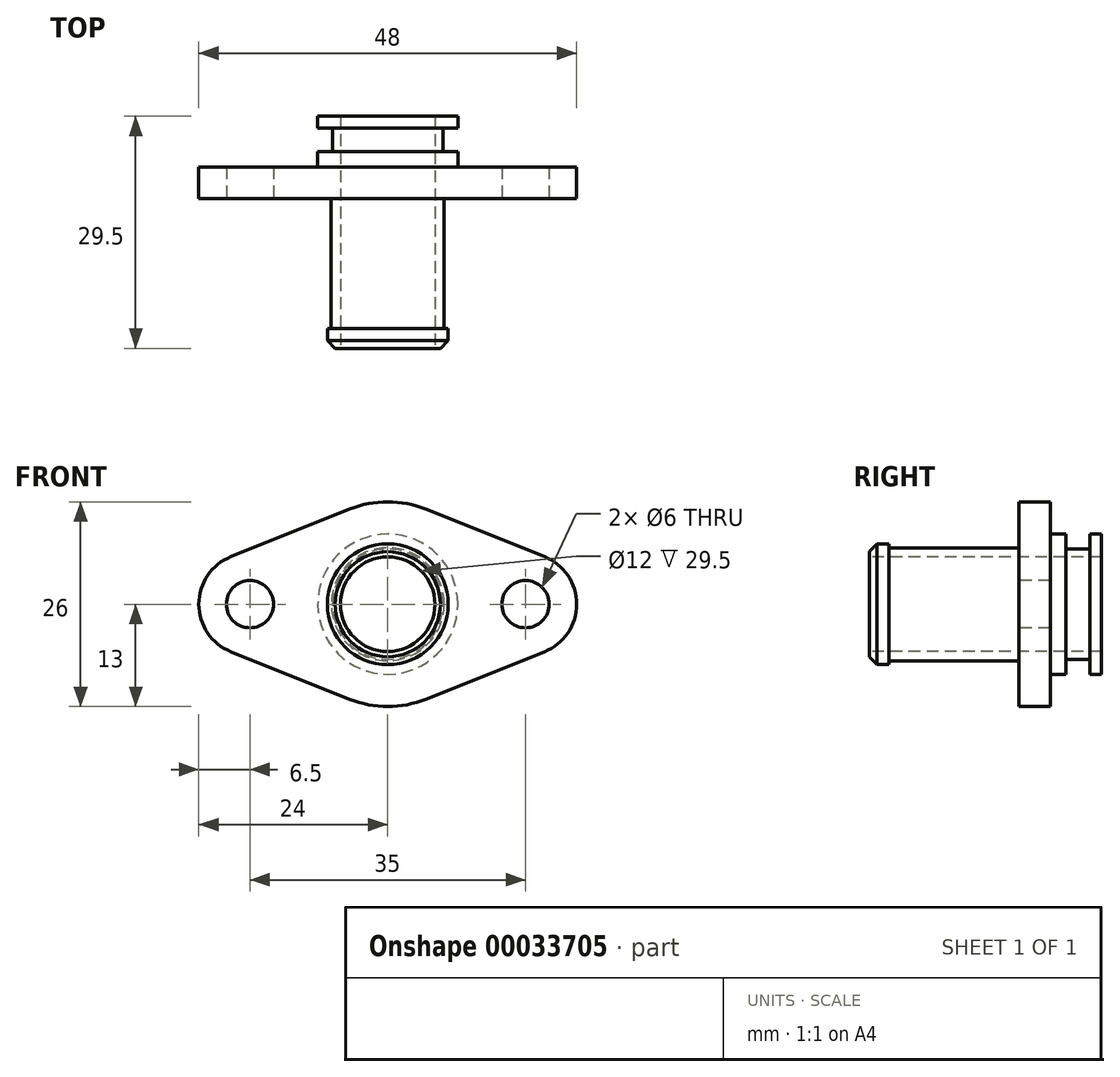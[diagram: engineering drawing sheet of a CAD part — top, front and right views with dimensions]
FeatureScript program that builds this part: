
annotation { "Feature Type Name" : "Feature", "Feature Type Description" : "" }
export const myFeature = defineFeature(function(context is Context, id is Id, definition is map)
    precondition{}
    {
        {
            var Q0;
            Q0=qCreatedBy(makeId("Right.planeOp"),FACE);
            var sketch = newSketch(context, id + "F0", { "sketchPlane" : qUnion([Q0])});
            skLineSegment(sketch, "E0", {"start": v(-19, 0) * mm, "end": v(11.7, 0) * mm, "construction": true});
            skLineSegment(sketch, "E1", {"start": v(-19, 6) * mm, "end": v(10.5, 6) * mm});
            skLineSegment(sketch, "E2", {"start": v(10.5, 6) * mm, "end": v(10.5, 8.9) * mm});
            skLineSegment(sketch, "E3", {"start": v(10.5, 8.9) * mm, "end": v(9, 8.9) * mm});
            skLineSegment(sketch, "E4", {"start": v(9, 8.9) * mm, "end": v(9, 7) * mm});
            skLineSegment(sketch, "E5", {"start": v(9, 7) * mm, "end": v(6, 7) * mm});
            skLineSegment(sketch, "E6", {"start": v(6, 7) * mm, "end": v(6, 8.9) * mm});
            skLineSegment(sketch, "E7", {"start": v(6, 8.9) * mm, "end": v(4, 8.9) * mm});
            skLineSegment(sketch, "E8", {"start": v(4, 8.9) * mm, "end": v(4, 24) * mm});
            skLineSegment(sketch, "E9", {"start": v(4, 24) * mm, "end": v(0, 24) * mm});
            skLineSegment(sketch, "E10", {"start": v(0, 24) * mm, "end": v(0, 7.17) * mm});
            skLineSegment(sketch, "E11", {"start": v(-16.5, 7.17) * mm, "end": v(-16.5, 7.67) * mm});
            skLineSegment(sketch, "E12", {"start": v(-16.5, 7.67) * mm, "end": v(-19, 7.67) * mm});
            skLineSegment(sketch, "E13", {"start": v(-19, 7.67) * mm, "end": v(-19, 6) * mm});
            skLineSegment(sketch, "E14", {"start": v(-16.5, 7.17) * mm, "end": v(0, 7.17) * mm});
            skSolve(sketch);
        }
        {
            var Q0;
            Q0 = qSketchRegion(id + "F0", true);
            var Q1;
            Q1=sQuery(id+"F0.wireOp",EDGE,"E0");
            revolve(context, id + "F1", {"entities" : qUnion([Q0]), "axis" : qUnion([Q1]), "revolveType" : RevolveType.FULL});
        }
        {
            var Q0;
            Q0=makeQuery(id+"F1.opRevolve","SWEPT_EDGE",EDGE,{"disambiguationData":[OSD([sQuery(id+"F0.wireOp",EDGE,"E12"),sQuery(id+"F0.wireOp",EDGE,"E13")])]});
            chamfer(context, id + "F2", {"entities" : qUnion([Q0]), "width" : 1 * mm, "tangentPropagation" : true});
        }
        {
            var Q0;
            Q0=makeQuery(id+"F1.opRevolve","SWEPT_FACE",FACE,{"disambiguationData":[OSD([sQuery(id+"F0.wireOp",EDGE,"E10")])]});
            var sketch = newSketch(context, id + "F3", { "sketchPlane" : qUnion([Q0])});
            skCircle(sketch, "E15", {"center": v(-17.5, 0) * mm, "radius": 3 * mm});
            skCircle(sketch, "E16", {"center": v(17.5, 0) * mm, "radius": 3 * mm});
            skCircle(sketch, "E17", {"center": v(0, 0) * mm, "radius": 17.5 * mm, "construction": true});
            skArc(sketch, "E18", {"start": v(-19.91, 6.03) * mm, "mid": v(-24, 0) * mm, "end": v(-19.91, -6.03) * mm});
            skArc(sketch, "E19", {"start": v(19.91, -6.03) * mm, "mid": v(24, 0) * mm, "end": v(19.91, 6.03) * mm});
            skLineSegment(sketch, "E20", {"start": v(-19.91, 6.03) * mm, "end": v(-4.83, 12.07) * mm});
            skLineSegment(sketch, "E21", {"start": v(-19.91, -6.03) * mm, "end": v(-4.83, -12.07) * mm});
            skLineSegment(sketch, "E22", {"start": v(4.83, 12.07) * mm, "end": v(19.91, 6.03) * mm});
            skLineSegment(sketch, "E23", {"start": v(4.83, -12.07) * mm, "end": v(19.91, -6.03) * mm});
            skArc(sketch, "E24.trimOffspring", {"start": v(-4.83, -12.07) * mm, "mid": v(0, -13) * mm, "end": v(4.83, -12.07) * mm});
            skArc(sketch, "E25.trimOffspring", {"start": v(4.83, 12.07) * mm, "mid": v(0, 13) * mm, "end": v(-4.83, 12.07) * mm});
            skCircle(sketch, "E26", {"center": v(0, 0) * mm, "radius": 30 * mm});
            skSolve(sketch);
        }
        {
            var Q0;
            Q0 = qSketchRegion(id + "F3", true);
            extrude(context, id + "F4", {"entities" : qUnion([Q0]), "operationType" : NewBodyOperationType.REMOVE, "oppositeDirection" : true, "depth" : 25 * mm});
        }
        {
            var Q0;
            Q0=makeQuery(id+"F3.imprint","IMPRINT",FACE,{"disambiguationData":[TD([[makeQuery(id+"F3.imprint","IMPRINT",EDGE,{"derivedFrom":sQuery(id+"F3.wireOp",EDGE,"E16")}),1.0]])]});
            var Q1;
            Q1=makeQuery(id+"F3.imprint","IMPRINT",FACE,{"disambiguationData":[TD([[makeQuery(id+"F3.imprint","IMPRINT",EDGE,{"derivedFrom":sQuery(id+"F3.wireOp",EDGE,"E15")}),1.0]])]});
            extrude(context, id + "F5", {"entities" : qUnion([Q0, Q1]), "operationType" : NewBodyOperationType.REMOVE, "oppositeDirection" : true, "depth" : 25 * mm});
        }
    });
